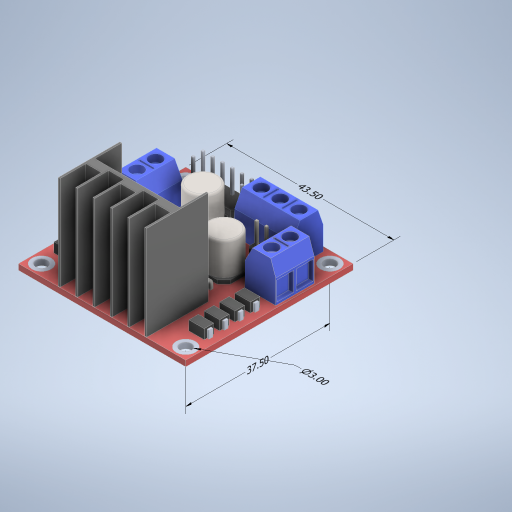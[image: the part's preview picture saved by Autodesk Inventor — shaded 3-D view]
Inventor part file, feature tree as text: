
AUTODESK INVENTOR PART (.ipt)
format: ipt  version: 2024 (Build 280153000, 153)  size: 809,984 bytes
history: native  units: mm
features: other x39, mirror x5, chamfer x1, sweep x1
ambient origin geometry x8: Origin, YZ Plane, XZ Plane, XY Plane, X Axis, Y Axis, Z Axis, Center Point
bodies: Body1 (feature_tree), Body2 (feature_tree), Body3 (feature_tree), Body4 (feature_tree), Body5 (feature_tree), Body6 (feature_tree), Body7 (feature_tree), Body8 (feature_tree), Body9 (feature_tree), Body10 (feature_tree), Body11 (feature_tree), Body12 (feature_tree), Body13 (feature_tree), Body14 (feature_tree), Body15 (feature_tree), Body16 (feature_tree), Body17 (feature_tree), Body18 (feature_tree), Body19 (feature_tree), Body20 (feature_tree), Body21 (feature_tree)
feature tree (46):
  other  "Sólido1"
  other  "Annotations"
  other  "Sólido2"
  other  "Sólido3"
  other  "Sólido4"
  other  "Sólido5"
  other  "Sólido6"
  other  "Sólido7"
  other  "Sólido8"
  other  "Sólido9"
  other  "Sólido10"
  other  "Sólido11"
  other  "Sólido12"
  other  "Sólido13"
  other  "Sólido14"
  other  "Sólido15"
  other  "Sólido16"
  other  "Sólido17"
  other  "Sólido18"
  other  "Sólido19"
  other  "Sólido20"
  other  "Sólido21"
  other  "Cut-Extrude1"
  other  "LPattern1[1]"
  other  "LPattern1[2]"
  other  "LPattern1[3]"
  chamfer  "Chamfer3"  [1 undecoded]
  other  "Diode"
  other  "LPattern3"
  mirror  "Mirror3[1]"
  mirror  "Mirror3[2]"
  mirror  "Mirror3[3]"
  mirror  "Mirror3[4]"
  sweep  "Sweep2"
  other  "capacitor"
  other  "LPattern6"
  other  "Cut-Extrude4"
  other  "Cut-Extrude7"
  mirror  "Mirror5"
  other  "Boss-Extrude15"
  other  "Boss-Extrude16[1]"
  other  "Boss-Extrude16[2]"
  other  "Boss-Extrude18"
  other  "Diameter Dimension 1"
  other  "Linear Dimension 1"
  other  "Linear Dimension 2"
note: 1 required parameter value undecoded (feature->parameter linkage not recoverable at this tier; creation-order binding heuristic only, values carry confidence <= 0.55)
